# Revit family: Urinal-TopInlet-Vitra_ArkitektSeries_6201
name_source: partatom
category: Plumbing Fixtures
revit_build: Autodesk Revit 2017 (Build: 20160225_1515(x64)
units: mm (PartAtom-declared; Revit-internal decimal feet)

## family parameters
Cut with Voids When Loaded = No
Host = Face
OmniClass Number = 23.45.05.14.14
OmniClass Title = Sinks/Lavatories
Part Type = Normal
Room Calculation Point = No
Round Connector Dimension = Use Diameter
Shared = Yes

## types (4) — shared parameters
BIMobject category = Urinals
Brand = VitrA
CW Connection = Yes
Color = White
Default Elevation = 650 mm  [stored 2.13255 ft]
Description = VitrA Arkitekt
Design country = Turkey
HW Connection = No
IFC Classification = Sanitary Terminal
Main Material = Ceramic
Manufacturer = Vitra
Manufacturer name = Vitra
Masterformat 2014 Code = 22 41 13.16
Masterformat 2014 Description = Residential Urinals
Mounting type = Wall Mounted Urinal
NBS Referans Code = 31-93
NBS Referans Description = Urinal And Wc Fittings
Nominal Depth (mm) = 310 mm  [stored 1.01706 ft]
Nominal Height (mm) = 570 mm
Nominal Width (mm) = 320 mm  [stored 1.04987 ft]
OmniClass Code = 23-31 21 00
OmniClass Description = Urinals
Primary Material = White
Product certification = https://www.vitraglobal.com
Product family = Wall Mounted Urinal
Product group = Arkitekt
Secondary Material = White
URL = https://www.vitra.com.tr
Uniclass 1.4 Code = L721
Uniclass 1.4 Description = Sanitary equipment
Uniclass 2.0 Code = PR-31-93
Uniclass 2.0 Description = Urinal And Wc Fittings
Uniclass 2015 Code = Pr_40_20_93
Uniclass 2015 Name = Urinal and WC fittings
Uniformat II Code = D2010
Uniformat II Description = Plumbing Fixtures
Vent Connection = No
Warranty Period (Year) = 10 Years
Waste Connection = Yes
Weight Net (kg) = 14.9
Youtube = https://www.youtube.com

## per-type parameters (varying)
| type | Article No. (default) | Model | Product SKU | Product url | Technical description |
| Urinal_Vitra_Arkitekt_6201B003H0199 | 6201B003H0199 | 6201B003H0199 | 6201B003H0199 | https://www.vitra-india.com | https://www.vitra-india.com |
| Urinal_Vitra_Arkitekt_6201L003D0201 | 6201L003D0201 | 6201L003D0201 | 6201L003D0201 | https://www.vitraglobal.com | https://www.vitraglobal.com |
| Urinal_Vitra_Arkitekt_6201B403-0199 | 6201B403-0199 | 6201B403-0199 | 6201B403-0199 | https://www.vitraglobal.com | https://www.vitraglobal.com |
| Urinal_Vitra_Arkitekt_6201B003-0199 | 6201B003-0199 | 6201B003-0199 | 6201B003-0199 | https://www.vitraglobal.com | https://www.vitraglobal.com |

note: [stored X ft] marks values corroborated as IEEE doubles in the binary element streams (Revit-internal decimal feet)

## geometry (parser evidence)
native form markers: Sweep x2
no freeform markers — native parametric forms only
